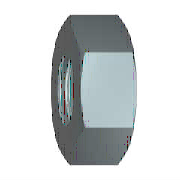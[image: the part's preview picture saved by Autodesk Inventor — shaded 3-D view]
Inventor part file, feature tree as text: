
AUTODESK INVENTOR PART (.ipt)
format: ipt  version: 2015 (Build 190159000, 159)  size: 164,352 bytes
history: native  units: mm (DEFAULTED — no unit token found)
features: sketch x3, other x2, extrude x1, hole x1, plane x1
ambient origin geometry x7: Origin, YZ Plane, XZ Plane, X Axis, Y Axis, Z Axis, Center Point
bodies: Body1 (feature_tree)
feature tree (8):
  extrude  "Bryła"  Depth=18.475209mm
  other  "Faza1"
  hole  "Gwint"  [1 undecoded]
  other  "Work Axis1"
  plane  "Work Plane1"
  sketch  "Szkic1"
  sketch  "Szkic2"
  sketch  "Szkic3"
note: 1 required parameter value undecoded (feature->parameter linkage not recoverable at this tier; creation-order binding heuristic only, values carry confidence <= 0.55)
